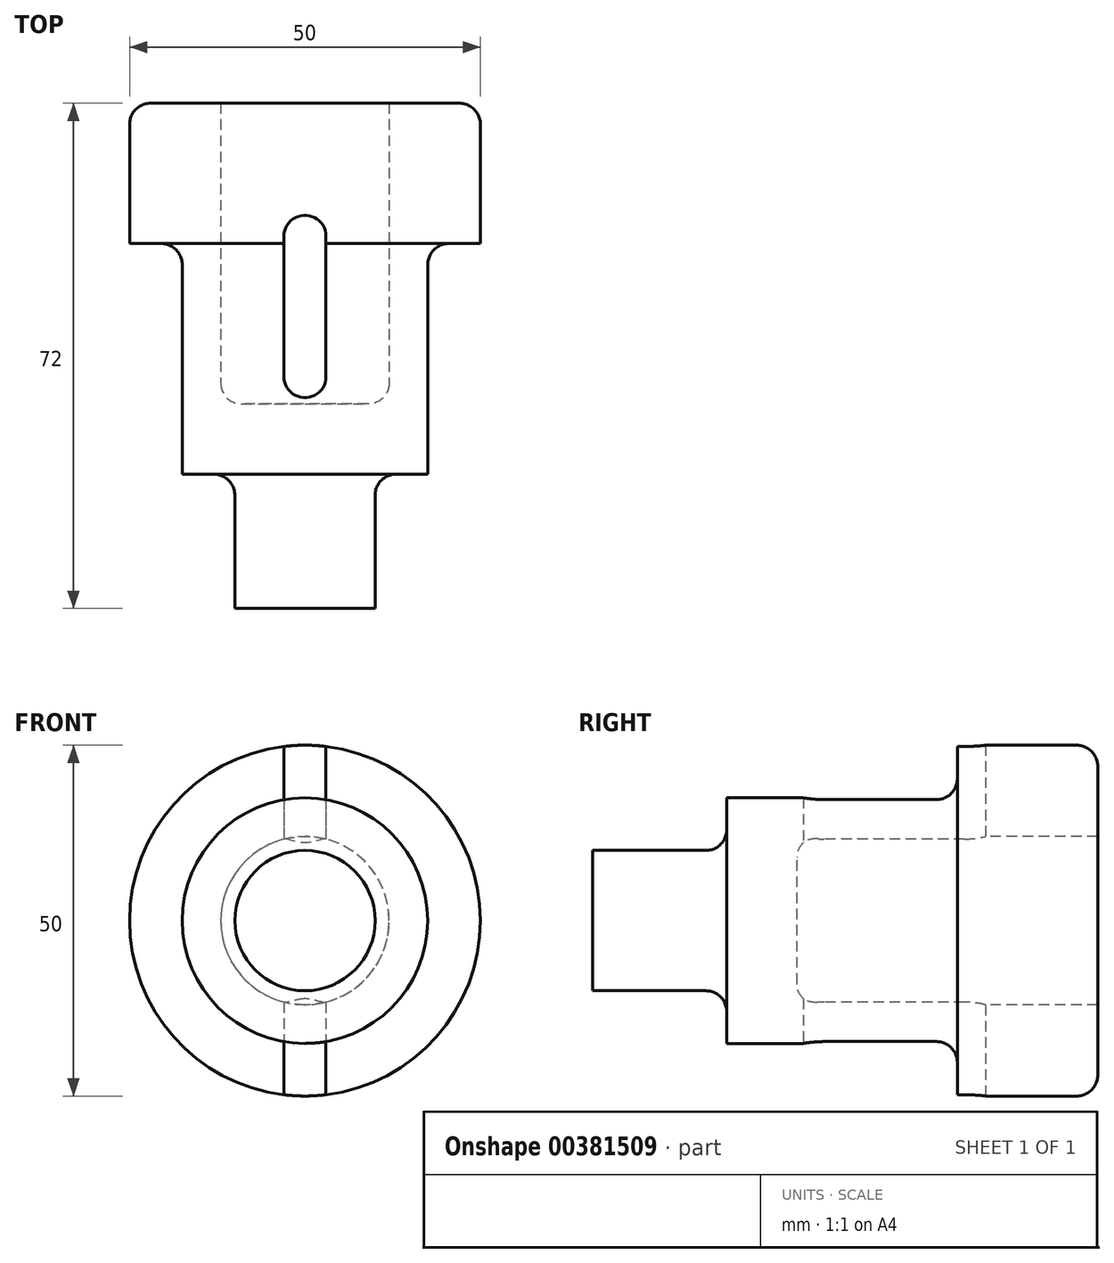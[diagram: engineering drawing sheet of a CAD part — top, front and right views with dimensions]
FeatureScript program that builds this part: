
annotation { "Feature Type Name" : "Feature", "Feature Type Description" : "" }
export const myFeature = defineFeature(function(context is Context, id is Id, definition is map)
    precondition{}
    {
        {
            var Q0;
            Q0=qCreatedBy(makeId("Right.planeOp"),FACE);
            var sketch = newSketch(context, id + "F0", { "sketchPlane" : qUnion([Q0])});
            skLineSegment(sketch, "E0", {"start": v(0, 0) * mm, "end": v(0, 10) * mm});
            skLineSegment(sketch, "E1", {"start": v(0, 10) * mm, "end": v(16.13, 10) * mm});
            skLineSegment(sketch, "E2", {"start": v(19.13, 13) * mm, "end": v(19.13, 17.5) * mm});
            skLineSegment(sketch, "E3", {"start": v(19.13, 17.5) * mm, "end": v(49, 17.5) * mm});
            skLineSegment(sketch, "E4", {"start": v(52, 20.5) * mm, "end": v(52, 25) * mm});
            skLineSegment(sketch, "E5", {"start": v(52, 25) * mm, "end": v(69, 25) * mm});
            skLineSegment(sketch, "E6", {"start": v(72, 22) * mm, "end": v(72, 12) * mm});
            skLineSegment(sketch, "E7", {"start": v(29.13, 0) * mm, "end": v(29.13, 9) * mm});
            skLineSegment(sketch, "E8", {"start": v(32.13, 12) * mm, "end": v(72, 12) * mm});
            skPoint(sketch, "E9.visualSharp", {"position": v(19.13, 10) * mm});
            skArc(sketch, "E9.filletArc", {"start": v(16.13, 10) * mm, "mid": v(18.25, 10.88) * mm, "end": v(19.13, 13) * mm});
            skPoint(sketch, "E10.visualSharp", {"position": v(29.13, 12) * mm});
            skArc(sketch, "E10.filletArc", {"start": v(32.13, 12) * mm, "mid": v(30, 11.12) * mm, "end": v(29.13, 9) * mm});
            skPoint(sketch, "E11.visualSharp", {"position": v(52, 17.5) * mm});
            skArc(sketch, "E11.filletArc", {"start": v(49, 17.5) * mm, "mid": v(51.12, 18.38) * mm, "end": v(52, 20.5) * mm});
            skPoint(sketch, "E12.visualSharp", {"position": v(72, 25) * mm});
            skArc(sketch, "E12.filletArc", {"start": v(72, 22) * mm, "mid": v(71.12, 24.12) * mm, "end": v(69, 25) * mm});
            skLineSegment(sketch, "E13", {"start": v(0, 0) * mm, "end": v(29.13, 0) * mm});
            skSolve(sketch);
        }
        {
            var Q0;
            Q0=makeQuery(id+"F0.imprint","IMPRINT",FACE,{"disambiguationData":[TD([[makeQuery(id+"F0.imprint","IMPRINT",EDGE,{"derivedFrom":sQuery(id+"F0.wireOp",EDGE,"E0")}),-1.0]])]});
            var Q1;
            Q1=sQuery(id+"F0.wireOp",EDGE,"E13");
            revolve(context, id + "F1", {"entities" : qUnion([Q0]), "axis" : qUnion([Q1]), "revolveType" : RevolveType.FULL});
        }
        {
            var Q0;
            Q0=qCreatedBy(makeId("Top.planeOp"),FACE);
            var sketch = newSketch(context, id + "F2", { "sketchPlane" : qUnion([Q0])});
            skLineSegment(sketch, "E14", {"start": v(-3, 53.03) * mm, "end": v(-3, 33.03) * mm});
            skLineSegment(sketch, "E15.MirrorCS", {"start": v(3, 53.03) * mm, "end": v(3, 33.03) * mm});
            skLineSegment(sketch, "E16", {"start": v(0, 56.03) * mm, "end": v(0, 56.03) * mm});
            skLineSegment(sketch, "E17", {"start": v(0, 30.03) * mm, "end": v(0, 30.03) * mm});
            skPoint(sketch, "E18.visualSharp", {"position": v(3, 30.03) * mm});
            skArc(sketch, "E18.filletArc", {"start": v(0, 30.03) * mm, "mid": v(2.12, 30.91) * mm, "end": v(3, 33.03) * mm});
            skPoint(sketch, "E19.visualSharp", {"position": v(-3, 30.03) * mm});
            skArc(sketch, "E19.filletArc", {"start": v(-3, 33.03) * mm, "mid": v(-2.12, 30.91) * mm, "end": v(0, 30.03) * mm});
            skPoint(sketch, "E20.visualSharp", {"position": v(3, 56.03) * mm});
            skArc(sketch, "E20.filletArc", {"start": v(3, 53.03) * mm, "mid": v(2.12, 55.15) * mm, "end": v(0, 56.03) * mm});
            skPoint(sketch, "E21.visualSharp", {"position": v(-3, 56.03) * mm});
            skArc(sketch, "E21.filletArc", {"start": v(0, 56.03) * mm, "mid": v(-2.12, 55.15) * mm, "end": v(-3, 53.03) * mm});
            skSolve(sketch);
        }
        {
            var Q0;
            Q0=makeQuery(id+"F2.imprint","IMPRINT",FACE,{"disambiguationData":[TD([[makeQuery(id+"F2.imprint","IMPRINT",EDGE,{"derivedFrom":sQuery(id+"F2.wireOp",EDGE,"E14")}),1.0]])]});
            extrude(context, id + "F3", {"entities" : qUnion([Q0]), "operationType" : NewBodyOperationType.REMOVE, "endBound" : BoundingType.SYMMETRIC, "depth" : 65 * mm});
        }
    });
